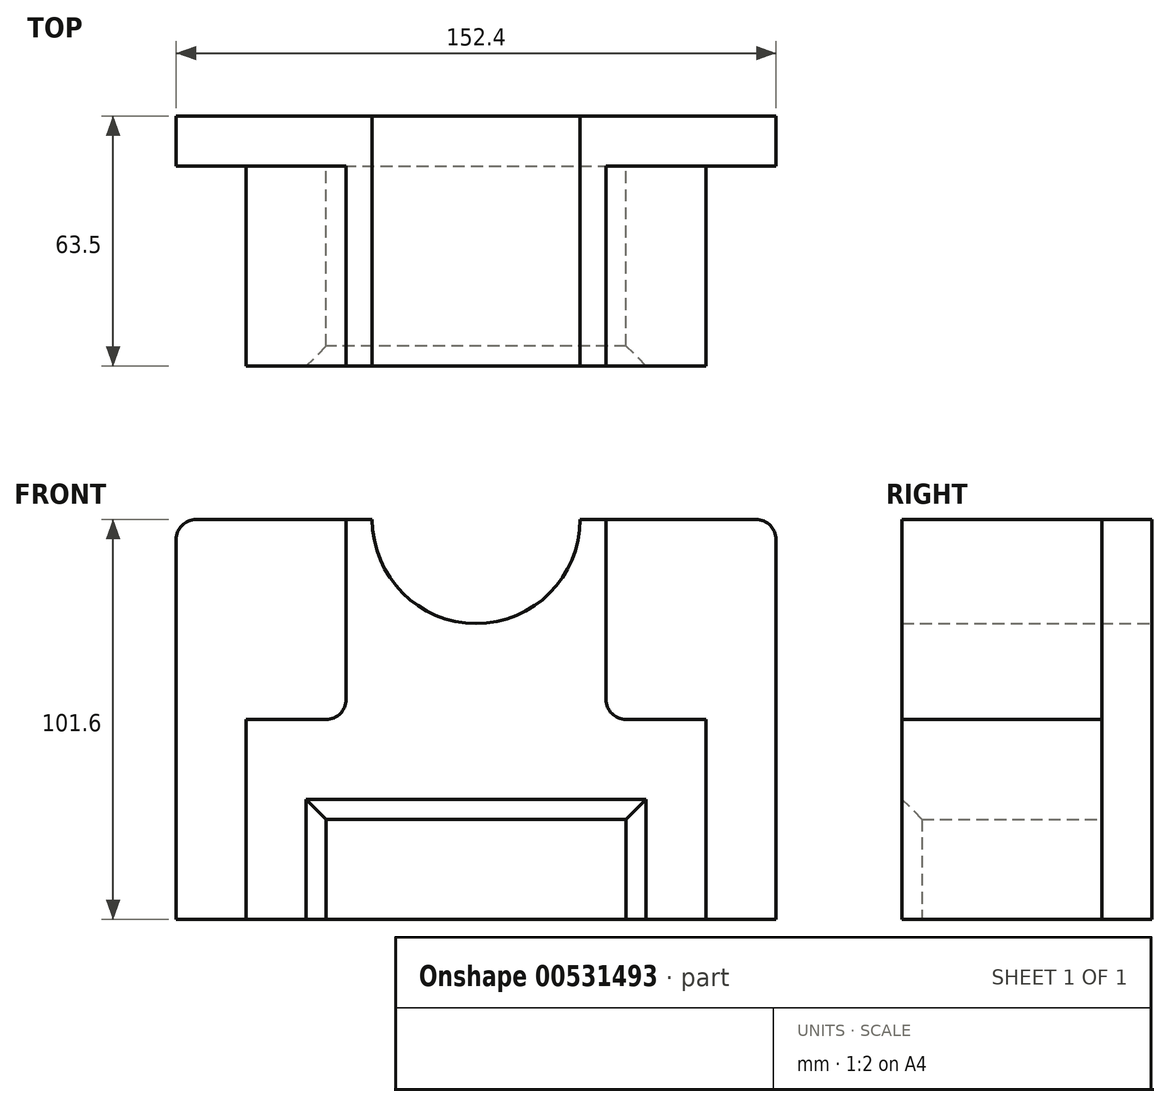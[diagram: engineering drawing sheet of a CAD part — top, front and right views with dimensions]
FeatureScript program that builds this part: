
annotation { "Feature Type Name" : "Feature", "Feature Type Description" : "" }
export const myFeature = defineFeature(function(context is Context, id is Id, definition is map)
    precondition{}
    {
        {
            var Q0;
            Q0=qCreatedBy(makeId("Front.planeOp"),FACE);
            var sketch = newSketch(context, id + "F0", { "sketchPlane" : qUnion([Q0])});
            skLineSegment(sketch, "E0.bottom", {"start": v(76.2, -50.8) * mm, "end": v(-76.2, -50.8) * mm});
            skLineSegment(sketch, "E0.top", {"start": v(76.2, 50.8) * mm, "end": v(-76.2, 50.8) * mm});
            skLineSegment(sketch, "E0.left", {"start": v(76.2, -50.8) * mm, "end": v(76.2, 50.8) * mm});
            skLineSegment(sketch, "E0.right", {"start": v(-76.2, -50.8) * mm, "end": v(-76.2, 50.8) * mm});
            skPoint(sketch, "E0.middle", {"position": v(0, 0) * mm});
            skSolve(sketch);
        }
        {
            var Q0;
            Q0=makeQuery(id+"F0.imprint","IMPRINT",FACE,{"disambiguationData":[TD([[makeQuery(id+"F0.imprint","IMPRINT",EDGE,{"derivedFrom":sQuery(id+"F0.wireOp",EDGE,"E0.bottom")}),-1.0]])]});
            extrude(context, id + "F1", {"entities" : qUnion([Q0]), "depth" : 12.7 * mm, "offsetDistance" : 25.4 * mm});
        }
        {
            var Q0;
            Q0=makeQuery(id+"F1.opExtrude","CAP_FACE",FACE,{"disambiguationData":[OSD([sQuery(id+"F0.wireOp",EDGE,"E0.bottom"),sQuery(id+"F0.wireOp",EDGE,"E0.top"),sQuery(id+"F0.wireOp",EDGE,"E0.left"),sQuery(id+"F0.wireOp",EDGE,"E0.right")])],"isStart":false});
            var sketch = newSketch(context, id + "F2", { "sketchPlane" : qUnion([Q0])});
            skLineSegment(sketch, "E1", {"start": v(-33.02, 50.8) * mm, "end": v(-33.02, 0) * mm});
            skLineSegment(sketch, "E2", {"start": v(-33.02, 0) * mm, "end": v(-58.42, 0) * mm});
            skLineSegment(sketch, "E3", {"start": v(-58.42, 0) * mm, "end": v(-58.42, -50.8) * mm});
            skLineSegment(sketch, "E4", {"start": v(-58.42, -50.8) * mm, "end": v(-38.1, -50.8) * mm});
            skLineSegment(sketch, "E5", {"start": v(-38.1, -50.8) * mm, "end": v(-38.1, -25.4) * mm});
            skLineSegment(sketch, "E6", {"start": v(-38.1, -25.4) * mm, "end": v(38.1, -25.4) * mm});
            skLineSegment(sketch, "E7", {"start": v(38.1, -25.4) * mm, "end": v(38.1, -50.8) * mm});
            skLineSegment(sketch, "E8", {"start": v(38.1, -50.8) * mm, "end": v(58.42, -50.8) * mm});
            skLineSegment(sketch, "E9", {"start": v(58.42, -50.8) * mm, "end": v(58.42, 0) * mm});
            skLineSegment(sketch, "E10", {"start": v(58.42, 0) * mm, "end": v(33.02, 0) * mm});
            skLineSegment(sketch, "E11", {"start": v(33.02, 0) * mm, "end": v(33.02, 50.8) * mm});
            skLineSegment(sketch, "E12", {"start": v(33.02, 50.8) * mm, "end": v(-33.02, 50.8) * mm});
            skSolve(sketch);
        }
        {
            var Q0;
            Q0 = qSketchRegion(id + "F2", true);
            extrude(context, id + "F3", {"entities" : qUnion([Q0]), "operationType" : NewBodyOperationType.ADD, "depth" : 50.8 * mm, "offsetDistance" : 25.4 * mm});
        }
        {
            var Q0;
            Q0=makeQuery(id+"F1.opExtrude","SWEPT_EDGE",EDGE,{"disambiguationData":[OSD([sQuery(id+"F0.wireOp",EDGE,"E0.top"),sQuery(id+"F0.wireOp",EDGE,"E0.left")])]});
            fillet(context, id + "F4", {"entities" : qUnion([Q0]), "radius" : 5.08 * mm, "tangentPropagation" : true, "allowEdgeOverflow" : false});
        }
        {
            var Q0;
            Q0=makeQuery(id+"F1.opExtrude","SWEPT_EDGE",EDGE,{"disambiguationData":[OSD([sQuery(id+"F0.wireOp",EDGE,"E0.top"),sQuery(id+"F0.wireOp",EDGE,"E0.right")])]});
            fillet(context, id + "F5", {"entities" : qUnion([Q0]), "radius" : 5.08 * mm, "tangentPropagation" : true, "allowEdgeOverflow" : false});
        }
        {
            var Q0;
            Q0=makeQuery(id+"F3.opExtrude","SWEPT_EDGE",EDGE,{"disambiguationData":[OSD([sQuery(id+"F2.wireOp",EDGE,"E10"),sQuery(id+"F2.wireOp",EDGE,"E11")])]});
            fillet(context, id + "F6", {"entities" : qUnion([Q0]), "radius" : 5.08 * mm, "tangentPropagation" : true, "allowEdgeOverflow" : false});
        }
        {
            var Q0;
            Q0=makeQuery(id+"F3.opExtrude","SWEPT_EDGE",EDGE,{"disambiguationData":[OSD([sQuery(id+"F2.wireOp",EDGE,"E1"),sQuery(id+"F2.wireOp",EDGE,"E2")])]});
            fillet(context, id + "F7", {"entities" : qUnion([Q0]), "radius" : 5.08 * mm, "tangentPropagation" : true, "allowEdgeOverflow" : false});
        }
        {
            var Q0;
            Q0=qCreatedBy(makeId("Front.planeOp"),FACE);
            var sketch = newSketch(context, id + "F8", { "sketchPlane" : qUnion([Q0])});
            skCircle(sketch, "E13", {"center": v(0, 50.8) * mm, "radius": 26.41 * mm});
            skSolve(sketch);
        }
        {
            var Q0;
            Q0=makeQuery(id+"F8.imprint","IMPRINT",FACE,{"disambiguationData":[TD([[makeQuery(id+"F8.imprint","IMPRINT",EDGE,{"derivedFrom":sQuery(id+"F8.wireOp",EDGE,"E13")}),1.0]])]});
            extrude(context, id + "F9", {"entities" : qUnion([Q0]), "operationType" : NewBodyOperationType.REMOVE, "endBound" : BoundingType.THROUGH_ALL, "depth" : 25.4 * mm, "offsetDistance" : 25.4 * mm});
        }
        {
            var Q0;
            Q0=makeQuery(id+"F3.opExtrude","CAP_EDGE",EDGE,{"disambiguationData":[OSD([sQuery(id+"F2.wireOp",EDGE,"E6")])],"isStart":false});
            var Q1;
            Q1=makeQuery(id+"F3.opExtrude","CAP_EDGE",EDGE,{"disambiguationData":[OSD([sQuery(id+"F2.wireOp",EDGE,"E5")])],"isStart":false});
            var Q2;
            Q2=makeQuery(id+"F3.opExtrude","CAP_EDGE",EDGE,{"disambiguationData":[OSD([sQuery(id+"F2.wireOp",EDGE,"E7")])],"isStart":false});
            chamfer(context, id + "F10", {"entities" : qUnion([Q0, Q1, Q2]), "width" : 5.08 * mm, "tangentPropagation" : true});
        }
    });
